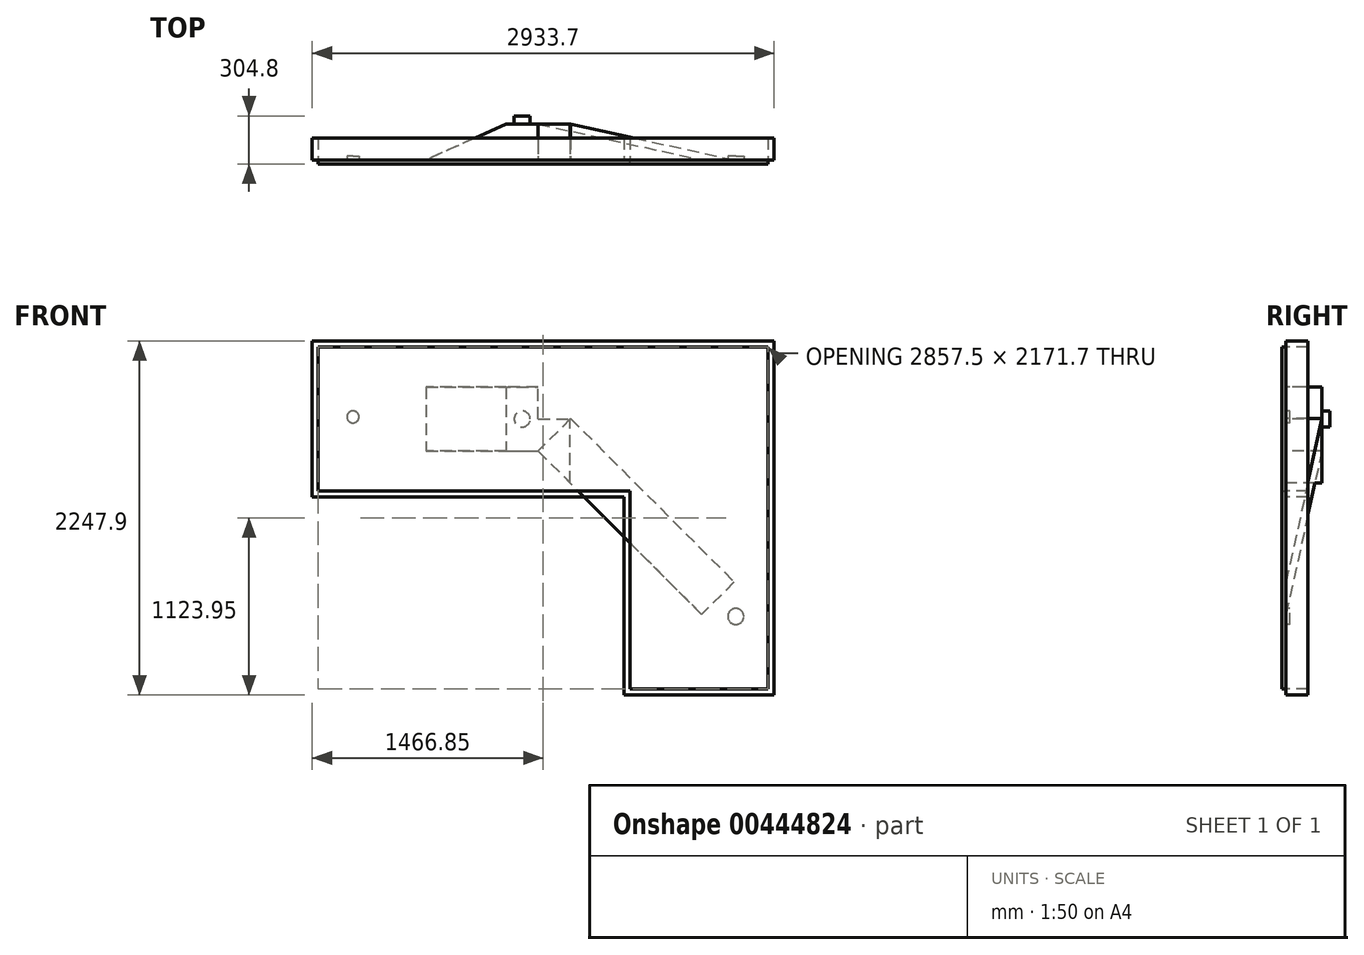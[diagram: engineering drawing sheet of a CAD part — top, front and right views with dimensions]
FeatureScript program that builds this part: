
annotation { "Feature Type Name" : "Feature", "Feature Type Description" : "" }
export const myFeature = defineFeature(function(context is Context, id is Id, definition is map)
    precondition{}
    {
        {
            var Q0;
            Q0=qCreatedBy(makeId("Front.planeOp"),FACE);
            var sketch = newSketch(context, id + "F0", { "sketchPlane" : qUnion([Q0])});
            skLineSegment(sketch, "E0", {"start": v(0, 0) * mm, "end": v(0, -914.4) * mm});
            skLineSegment(sketch, "E1", {"start": v(0, -914.4) * mm, "end": v(0, -952.5) * mm});
            skLineSegment(sketch, "E2", {"start": v(0, -952.5) * mm, "end": v(152.4, -952.5) * mm});
            skLineSegment(sketch, "E3", {"start": v(152.4, -952.5) * mm, "end": v(152.4, 0) * mm});
            skLineSegment(sketch, "E4", {"start": v(152.4, 0) * mm, "end": v(0, 0) * mm});
            skLineSegment(sketch, "E5", {"start": v(152.4, 0) * mm, "end": v(152.4, 38.1) * mm});
            skLineSegment(sketch, "E6", {"start": v(152.4, 38.1) * mm, "end": v(0, 38.1) * mm});
            skLineSegment(sketch, "E7", {"start": v(0, 38.1) * mm, "end": v(0, 0) * mm});
            skLineSegment(sketch, "E8", {"start": v(0, 38.1) * mm, "end": v(-38.1, 38.1) * mm});
            skLineSegment(sketch, "E9", {"start": v(-38.1, 38.1) * mm, "end": v(-38.1, -952.5) * mm});
            skLineSegment(sketch, "E10", {"start": v(-38.1, -952.5) * mm, "end": v(0, -952.5) * mm});
            skLineSegment(sketch, "E11", {"start": v(0, -914.4) * mm, "end": v(152.4, -914.4) * mm});
            skSolve(sketch);
        }
        {
            var Q0;
            Q0=makeQuery(id+"F0.imprint","IMPRINT",FACE,{"disambiguationData":[TD([[makeQuery(id+"F0.imprint","IMPRINT",EDGE,{"derivedFrom":sQuery(id+"F0.wireOp",EDGE,"E1")}),1.0]])]});
            var Q1;
            Q1=makeQuery(id+"F0.imprint","IMPRINT",FACE,{"disambiguationData":[TD([[makeQuery(id+"F0.imprint","IMPRINT",EDGE,{"derivedFrom":sQuery(id+"F0.wireOp",EDGE,"E0")}),-1.0]])]});
            var Q2;
            Q2=makeQuery(id+"F0.imprint","IMPRINT",FACE,{"disambiguationData":[TD([[makeQuery(id+"F0.imprint","IMPRINT",EDGE,{"derivedFrom":sQuery(id+"F0.wireOp",EDGE,"E4")}),-1.0]])]});
            extrude(context, id + "F1", {"entities" : qUnion([Q0, Q1, Q2]), "oppositeDirection" : true, "depth" : 139.7 * mm});
        }
        {
            var Q0;
            Q0=makeQuery(id+"F1.opExtrude","CAP_FACE",FACE,{"disambiguationData":[OSD([sQuery(id+"F0.wireOp",EDGE,"E0"),sQuery(id+"F0.wireOp",EDGE,"E2"),sQuery(id+"F0.wireOp",EDGE,"E3"),sQuery(id+"F0.wireOp",EDGE,"E4"),sQuery(id+"F0.wireOp",EDGE,"E5"),sQuery(id+"F0.wireOp",EDGE,"E6"),sQuery(id+"F0.wireOp",EDGE,"E8"),sQuery(id+"F0.wireOp",EDGE,"E9"),sQuery(id+"F0.wireOp",EDGE,"E10"),sQuery(id+"F0.wireOp",EDGE,"E11")])],"isStart":true});
            var sketch = newSketch(context, id + "F2", { "sketchPlane" : qUnion([Q0])});
            skLineSegment(sketch, "E12", {"start": v(152.4, 38.1) * mm, "end": v(152.4, 0) * mm});
            skLineSegment(sketch, "E13", {"start": v(152.4, 0) * mm, "end": v(2895.6, 0) * mm});
            skLineSegment(sketch, "E14", {"start": v(2895.6, 0) * mm, "end": v(2895.6, 38.1) * mm});
            skLineSegment(sketch, "E15", {"start": v(2895.6, 38.1) * mm, "end": v(152.4, 38.1) * mm});
            skLineSegment(sketch, "E16", {"start": v(2895.6, 0) * mm, "end": v(2895.6, -914.4) * mm});
            skLineSegment(sketch, "E17", {"start": v(2895.6, -914.4) * mm, "end": v(2895.6, -952.5) * mm});
            skLineSegment(sketch, "E18", {"start": v(2895.6, -952.5) * mm, "end": v(152.4, -952.5) * mm});
            skLineSegment(sketch, "E19", {"start": v(152.4, -952.5) * mm, "end": v(152.4, -914.4) * mm});
            skLineSegment(sketch, "E20", {"start": v(152.4, -914.4) * mm, "end": v(2895.6, -914.4) * mm});
            skLineSegment(sketch, "E21", {"start": v(2895.6, -914.4) * mm, "end": v(2857.5, -914.4) * mm});
            skLineSegment(sketch, "E22", {"start": v(2857.5, -914.4) * mm, "end": v(2857.5, 0) * mm});
            skLineSegment(sketch, "E23", {"start": v(2857.5, 0) * mm, "end": v(2895.6, 0) * mm});
            skSolve(sketch);
        }
        {
            var Q0;
            Q0=makeQuery(id+"F2.imprint","IMPRINT",FACE,{"disambiguationData":[TD([[makeQuery(id+"F2.imprint","IMPRINT",EDGE,{"derivedFrom":sQuery(id+"F2.wireOp",EDGE,"E16")}),-1.0]])]});
            var Q1;
            Q1=makeQuery(id+"F2.imprint","IMPRINT",FACE,{"disambiguationData":[TD([[makeQuery(id+"F2.imprint","IMPRINT",EDGE,{"derivedFrom":sQuery(id+"F2.wireOp",EDGE,"E12")}),-1.0]])]});
            extrude(context, id + "F3", {"entities" : qUnion([Q0, Q1]), "operationType" : NewBodyOperationType.ADD, "oppositeDirection" : true, "depth" : 139.7 * mm});
        }
        {
            var Q0;
            Q0=makeQuery(id+"F3.boolean.opBoolean","MERGE",FACE,{"derivedFrom":[makeQuery(id+"F1.opExtrude","CAP_FACE",FACE,{"disambiguationData":[OSD([sQuery(id+"F0.wireOp",EDGE,"E0"),sQuery(id+"F0.wireOp",EDGE,"E2"),sQuery(id+"F0.wireOp",EDGE,"E3"),sQuery(id+"F0.wireOp",EDGE,"E4"),sQuery(id+"F0.wireOp",EDGE,"E5"),sQuery(id+"F0.wireOp",EDGE,"E6"),sQuery(id+"F0.wireOp",EDGE,"E8"),sQuery(id+"F0.wireOp",EDGE,"E9"),sQuery(id+"F0.wireOp",EDGE,"E10"),sQuery(id+"F0.wireOp",EDGE,"E11")])],"isStart":true}),makeQuery(id+"F3.opExtrude","CAP_FACE",FACE,{"disambiguationData":[OSD([sQuery(id+"F2.wireOp",EDGE,"E12"),sQuery(id+"F2.wireOp",EDGE,"E13"),sQuery(id+"F2.wireOp",EDGE,"E14"),sQuery(id+"F2.wireOp",EDGE,"E15"),sQuery(id+"F2.wireOp",EDGE,"E16"),sQuery(id+"F2.wireOp",EDGE,"E21"),sQuery(id+"F2.wireOp",EDGE,"E22")])],"isStart":true})]});
            var sketch = newSketch(context, id + "F4", { "sketchPlane" : qUnion([Q0])});
            skLineSegment(sketch, "E24", {"start": v(152.4, -952.5) * mm, "end": v(1981.2, -952.5) * mm});
            skLineSegment(sketch, "E25", {"start": v(1981.2, -952.5) * mm, "end": v(1981.2, -914.4) * mm});
            skLineSegment(sketch, "E26", {"start": v(1981.2, -914.4) * mm, "end": v(152.4, -914.4) * mm});
            skLineSegment(sketch, "E27", {"start": v(152.4, -914.4) * mm, "end": v(152.4, -952.5) * mm});
            skSolve(sketch);
        }
        {
            var Q0;
            Q0=makeQuery(id+"F4.imprint","IMPRINT",FACE,{"disambiguationData":[TD([[makeQuery(id+"F4.imprint","IMPRINT",EDGE,{"derivedFrom":sQuery(id+"F4.wireOp",EDGE,"E24")}),1.0]])]});
            extrude(context, id + "F5", {"entities" : qUnion([Q0]), "operationType" : NewBodyOperationType.ADD, "oppositeDirection" : true, "depth" : 139.7 * mm});
        }
        {
            var Q0;
            Q0=makeQuery(id+"F5.boolean.opBoolean","MERGE",FACE,{"derivedFrom":[makeQuery(id+"F3.boolean.opBoolean","MERGE",FACE,{"derivedFrom":[makeQuery(id+"F1.opExtrude","CAP_FACE",FACE,{"disambiguationData":[OSD([sQuery(id+"F0.wireOp",EDGE,"E0"),sQuery(id+"F0.wireOp",EDGE,"E2"),sQuery(id+"F0.wireOp",EDGE,"E3"),sQuery(id+"F0.wireOp",EDGE,"E4"),sQuery(id+"F0.wireOp",EDGE,"E5"),sQuery(id+"F0.wireOp",EDGE,"E6"),sQuery(id+"F0.wireOp",EDGE,"E8"),sQuery(id+"F0.wireOp",EDGE,"E9"),sQuery(id+"F0.wireOp",EDGE,"E10"),sQuery(id+"F0.wireOp",EDGE,"E11")])],"isStart":true}),makeQuery(id+"F3.opExtrude","CAP_FACE",FACE,{"disambiguationData":[OSD([sQuery(id+"F2.wireOp",EDGE,"E12"),sQuery(id+"F2.wireOp",EDGE,"E13"),sQuery(id+"F2.wireOp",EDGE,"E14"),sQuery(id+"F2.wireOp",EDGE,"E15"),sQuery(id+"F2.wireOp",EDGE,"E16"),sQuery(id+"F2.wireOp",EDGE,"E21"),sQuery(id+"F2.wireOp",EDGE,"E22")])],"isStart":true})]}),makeQuery(id+"F5.opExtrude","CAP_FACE",FACE,{"disambiguationData":[OSD([sQuery(id+"F4.wireOp",EDGE,"E24"),sQuery(id+"F4.wireOp",EDGE,"E25"),sQuery(id+"F4.wireOp",EDGE,"E26"),sQuery(id+"F4.wireOp",EDGE,"E27")])],"isStart":true})]});
            var sketch = newSketch(context, id + "F6", { "sketchPlane" : qUnion([Q0])});
            skLineSegment(sketch, "E28", {"start": v(1981.2, -952.5) * mm, "end": v(1981.2, -2171.7) * mm});
            skLineSegment(sketch, "E29", {"start": v(1981.2, -2171.7) * mm, "end": v(1943.1, -2171.7) * mm});
            skLineSegment(sketch, "E30", {"start": v(1943.1, -2171.7) * mm, "end": v(1943.1, -952.5) * mm});
            skLineSegment(sketch, "E31", {"start": v(1943.1, -952.5) * mm, "end": v(1981.2, -952.5) * mm});
            skLineSegment(sketch, "E32", {"start": v(1981.2, -2171.7) * mm, "end": v(2857.5, -2171.7) * mm});
            skLineSegment(sketch, "E33", {"start": v(2857.5, -2171.7) * mm, "end": v(2895.6, -2171.7) * mm});
            skLineSegment(sketch, "E34", {"start": v(2895.6, -2171.7) * mm, "end": v(2895.6, -914.4) * mm});
            skLineSegment(sketch, "E35", {"start": v(2895.6, -914.4) * mm, "end": v(2857.5, -914.4) * mm});
            skLineSegment(sketch, "E36", {"start": v(2857.5, -914.4) * mm, "end": v(2857.5, -2171.7) * mm});
            skLineSegment(sketch, "E37", {"start": v(1943.1, -2171.7) * mm, "end": v(1943.1, -2209.8) * mm});
            skLineSegment(sketch, "E38", {"start": v(1943.1, -2209.8) * mm, "end": v(2895.6, -2209.8) * mm});
            skLineSegment(sketch, "E39", {"start": v(2895.6, -2209.8) * mm, "end": v(2895.6, -2171.7) * mm});
            skSolve(sketch);
        }
        {
            var Q0;
            Q0=makeQuery(id+"F6.imprint","IMPRINT",FACE,{"disambiguationData":[TD([[makeQuery(id+"F6.imprint","IMPRINT",EDGE,{"derivedFrom":sQuery(id+"F6.wireOp",EDGE,"E33")}),1.0]])]});
            var Q1;
            Q1=makeQuery(id+"F6.imprint","IMPRINT",FACE,{"disambiguationData":[TD([[makeQuery(id+"F6.imprint","IMPRINT",EDGE,{"derivedFrom":sQuery(id+"F6.wireOp",EDGE,"E29")}),1.0]])]});
            var Q2;
            Q2=makeQuery(id+"F6.imprint","IMPRINT",FACE,{"disambiguationData":[TD([[makeQuery(id+"F6.imprint","IMPRINT",EDGE,{"derivedFrom":sQuery(id+"F6.wireOp",EDGE,"E28")}),-1.0]])]});
            extrude(context, id + "F7", {"entities" : qUnion([Q0, Q1, Q2]), "operationType" : NewBodyOperationType.ADD, "oppositeDirection" : true, "depth" : 139.7 * mm});
        }
        {
            var Q0;
            Q0=makeQuery(id+"F7.boolean.opBoolean","MERGE",FACE,{"derivedFrom":[makeQuery(id+"F5.boolean.opBoolean","MERGE",FACE,{"derivedFrom":[makeQuery(id+"F3.boolean.opBoolean","MERGE",FACE,{"derivedFrom":[makeQuery(id+"F1.opExtrude","CAP_FACE",FACE,{"disambiguationData":[OSD([sQuery(id+"F0.wireOp",EDGE,"E0"),sQuery(id+"F0.wireOp",EDGE,"E2"),sQuery(id+"F0.wireOp",EDGE,"E3"),sQuery(id+"F0.wireOp",EDGE,"E4"),sQuery(id+"F0.wireOp",EDGE,"E5"),sQuery(id+"F0.wireOp",EDGE,"E6"),sQuery(id+"F0.wireOp",EDGE,"E8"),sQuery(id+"F0.wireOp",EDGE,"E9"),sQuery(id+"F0.wireOp",EDGE,"E10"),sQuery(id+"F0.wireOp",EDGE,"E11")])],"isStart":true}),makeQuery(id+"F3.opExtrude","CAP_FACE",FACE,{"disambiguationData":[OSD([sQuery(id+"F2.wireOp",EDGE,"E12"),sQuery(id+"F2.wireOp",EDGE,"E13"),sQuery(id+"F2.wireOp",EDGE,"E14"),sQuery(id+"F2.wireOp",EDGE,"E15"),sQuery(id+"F2.wireOp",EDGE,"E16"),sQuery(id+"F2.wireOp",EDGE,"E21"),sQuery(id+"F2.wireOp",EDGE,"E22")])],"isStart":true})]}),makeQuery(id+"F5.opExtrude","CAP_FACE",FACE,{"disambiguationData":[OSD([sQuery(id+"F4.wireOp",EDGE,"E24"),sQuery(id+"F4.wireOp",EDGE,"E25"),sQuery(id+"F4.wireOp",EDGE,"E26"),sQuery(id+"F4.wireOp",EDGE,"E27")])],"isStart":true})]}),makeQuery(id+"F7.opExtrude","CAP_FACE",FACE,{"disambiguationData":[OSD([sQuery(id+"F6.wireOp",EDGE,"E28"),sQuery(id+"F6.wireOp",EDGE,"E30"),sQuery(id+"F6.wireOp",EDGE,"E31"),sQuery(id+"F6.wireOp",EDGE,"E32"),sQuery(id+"F6.wireOp",EDGE,"E34"),sQuery(id+"F6.wireOp",EDGE,"E35"),sQuery(id+"F6.wireOp",EDGE,"E36"),sQuery(id+"F6.wireOp",EDGE,"E37"),sQuery(id+"F6.wireOp",EDGE,"E38"),sQuery(id+"F6.wireOp",EDGE,"E39")])],"isStart":true})]});
            var sketch = newSketch(context, id + "F8", { "sketchPlane" : qUnion([Q0])});
            skLineSegment(sketch, "E40", {"start": v(2895.6, 38.1) * mm, "end": v(-38.1, 38.1) * mm});
            skLineSegment(sketch, "E41", {"start": v(-38.1, 38.1) * mm, "end": v(-38.1, -952.5) * mm});
            skLineSegment(sketch, "E42", {"start": v(-38.1, -952.5) * mm, "end": v(1943.1, -952.5) * mm});
            skLineSegment(sketch, "E43", {"start": v(1943.1, -952.5) * mm, "end": v(1943.1, -2209.8) * mm});
            skLineSegment(sketch, "E44", {"start": v(1943.1, -2209.8) * mm, "end": v(2895.6, -2209.8) * mm});
            skLineSegment(sketch, "E45", {"start": v(2895.6, -2209.8) * mm, "end": v(2895.6, 38.1) * mm});
            skSolve(sketch);
        }
        {
            var Q0;
            Q0=makeQuery(id+"F8.imprint","IMPRINT",FACE,{"disambiguationData":[TD([[makeQuery(id+"F8.imprint","IMPRINT",EDGE,{"derivedFrom":makeQuery(id+"F1.opExtrude","CAP_EDGE",EDGE,{"disambiguationData":[OSD([sQuery(id+"F0.wireOp",EDGE,"E0")])],"isStart":true})}),1.0]])]});
            extrude(context, id + "F9", {"entities" : qUnion([Q0]), "depth" : 25.4 * mm});
        }
        {
            var Q0;
            Q0=makeQuery(id+"F5.boolean.opBoolean","MERGE",FACE,{"derivedFrom":[makeQuery(id+"F1.opExtrude","SWEPT_FACE",FACE,{"disambiguationData":[OSD([sQuery(id+"F0.wireOp",EDGE,"E11")])]}),makeQuery(id+"F5.opExtrude","SWEPT_FACE",FACE,{"disambiguationData":[OSD([sQuery(id+"F4.wireOp",EDGE,"E26")])]})]});
            var sketch = newSketch(context, id + "F10", { "sketchPlane" : qUnion([Q0])});
            skLineSegment(sketch, "E46", {"start": v(0, 0) * mm, "end": v(990.6, 0) * mm});
            skLineSegment(sketch, "E47", {"start": v(990.6, 0) * mm, "end": v(1193.8, 0) * mm});
            skLineSegment(sketch, "E48", {"start": v(1193.8, 0) * mm, "end": v(685.8, 0) * mm});
            skLineSegment(sketch, "E49", {"start": v(1193.8, 0) * mm, "end": v(1193.8, 228.6) * mm});
            skLineSegment(sketch, "E50", {"start": v(1193.8, 228.6) * mm, "end": v(685.8, 0) * mm});
            skSolve(sketch);
        }
        {
            var Q0;
            Q0 = qSketchRegion(id + "F10", true);
            extrude(context, id + "F11", {"entities" : qUnion([Q0]), "operationType" : NewBodyOperationType.ADD, "depth" : 660.4 * mm, "hasSecondDirection" : true, "secondDirectionOppositeDirection" : false, "secondDirectionDepth" : 254 * mm});
        }
        {
            var Q0;
            Q0=makeQuery(id+"F9.opExtrude","CAP_FACE",FACE,{"disambiguationData":[OSD([sQuery(id+"F0.wireOp",EDGE,"E0"),sQuery(id+"F0.wireOp",EDGE,"E4"),sQuery(id+"F0.wireOp",EDGE,"E11"),sQuery(id+"F2.wireOp",EDGE,"E13"),sQuery(id+"F2.wireOp",EDGE,"E22"),sQuery(id+"F4.wireOp",EDGE,"E25"),sQuery(id+"F4.wireOp",EDGE,"E26"),sQuery(id+"F6.wireOp",EDGE,"E28"),sQuery(id+"F6.wireOp",EDGE,"E32"),sQuery(id+"F6.wireOp",EDGE,"E36")])],"isStart":true});
            var sketch = newSketch(context, id + "F12", { "sketchPlane" : qUnion([Q0])});
            skLineSegment(sketch, "E51", {"start": v(-1193.8, -660.4) * mm, "end": v(-1320.8, -660.4) * mm});
            skLineSegment(sketch, "E52", {"start": v(-1320.8, -660.4) * mm, "end": v(-1397, -660.4) * mm});
            skLineSegment(sketch, "E53", {"start": v(-1397, -660.4) * mm, "end": v(-1397, -254) * mm});
            skLineSegment(sketch, "E54", {"start": v(-1397, -254) * mm, "end": v(-1193.8, -254) * mm});
            skLineSegment(sketch, "E55", {"start": v(-1193.8, -254) * mm, "end": v(-1193.8, -660.4) * mm});
            skSolve(sketch);
        }
        {
            var Q0;
            Q0 = qSketchRegion(id + "F12", true);
            extrude(context, id + "F13", {"entities" : qUnion([Q0]), "operationType" : NewBodyOperationType.ADD, "depth" : 228.6 * mm});
        }
        {
            var Q0;
            Q0=makeQuery(id+"F13.opExtrude","CAP_FACE",FACE,{"disambiguationData":[OSD([sQuery(id+"F12.wireOp",EDGE,"E51"),sQuery(id+"F12.wireOp",EDGE,"E52"),sQuery(id+"F12.wireOp",EDGE,"E53"),sQuery(id+"F12.wireOp",EDGE,"E54"),sQuery(id+"F12.wireOp",EDGE,"E55")])],"isStart":false});
            var sketch = newSketch(context, id + "F14", { "sketchPlane" : qUnion([Q0])});
            skLineSegment(sketch, "E56", {"start": v(-1193.8, -457.2) * mm, "end": v(-1397, -457.2) * mm});
            skCircle(sketch, "E57", {"center": v(-1295.4, -457.2) * mm, "radius": 50.8 * mm});
            skSolve(sketch);
        }
        {
            var Q0;
            Q0 = qSketchRegion(id + "F14", true);
            extrude(context, id + "F15", {"entities" : qUnion([Q0]), "operationType" : NewBodyOperationType.ADD, "depth" : 50.8 * mm});
        }
        {
            var Q0;
            Q0=makeQuery(id+"F9.opExtrude","CAP_FACE",FACE,{"disambiguationData":[OSD([sQuery(id+"F0.wireOp",EDGE,"E0"),sQuery(id+"F0.wireOp",EDGE,"E4"),sQuery(id+"F0.wireOp",EDGE,"E11"),sQuery(id+"F2.wireOp",EDGE,"E13"),sQuery(id+"F2.wireOp",EDGE,"E22"),sQuery(id+"F4.wireOp",EDGE,"E25"),sQuery(id+"F4.wireOp",EDGE,"E26"),sQuery(id+"F6.wireOp",EDGE,"E28"),sQuery(id+"F6.wireOp",EDGE,"E32"),sQuery(id+"F6.wireOp",EDGE,"E36")])],"isStart":true});
            var sketch = newSketch(context, id + "F16", { "sketchPlane" : qUnion([Q0])});
            skLineSegment(sketch, "E58", {"start": v(-1397, -660.4) * mm, "end": v(-1397, -457.2) * mm});
            skLineSegment(sketch, "E59", {"start": v(-1397, -457.2) * mm, "end": v(-1600.2, -457.2) * mm});
            skLineSegment(sketch, "E60", {"start": v(-1600.2, -457.2) * mm, "end": v(-1397, -660.4) * mm});
            skSolve(sketch);
        }
        {
            var Q0;
            Q0=makeQuery(id+"F9.opExtrude","CAP_FACE",FACE,{"disambiguationData":[OSD([sQuery(id+"F0.wireOp",EDGE,"E0"),sQuery(id+"F0.wireOp",EDGE,"E4"),sQuery(id+"F0.wireOp",EDGE,"E11"),sQuery(id+"F2.wireOp",EDGE,"E13"),sQuery(id+"F2.wireOp",EDGE,"E22"),sQuery(id+"F4.wireOp",EDGE,"E25"),sQuery(id+"F4.wireOp",EDGE,"E26"),sQuery(id+"F6.wireOp",EDGE,"E28"),sQuery(id+"F6.wireOp",EDGE,"E32"),sQuery(id+"F6.wireOp",EDGE,"E36")])],"isStart":true});
            var sketch = newSketch(context, id + "F17", { "sketchPlane" : qUnion([Q0])});
            skLineSegment(sketch, "E61", {"start": v(-1600.2, -660.4) * mm, "end": v(-1600.2, -457.2) * mm});
            skLineSegment(sketch, "E62", {"start": v(-1397, -660.4) * mm, "end": v(-1600.2, -457.2) * mm});
            skLineSegment(sketch, "E63", {"start": v(-1397, -660.4) * mm, "end": v(-1600.2, -863.6) * mm});
            skLineSegment(sketch, "E64", {"start": v(-1600.2, -863.6) * mm, "end": v(-1600.2, -660.4) * mm});
            skSolve(sketch);
        }
        {
            var Q0;
            Q0 = qSketchRegion(id + "F16", true);
            extrude(context, id + "F18", {"entities" : qUnion([Q0]), "operationType" : NewBodyOperationType.ADD, "depth" : 228.6 * mm});
        }
        {
            var Q0;
            Q0 = qSketchRegion(id + "F17", true);
            extrude(context, id + "F19", {"entities" : qUnion([Q0]), "operationType" : NewBodyOperationType.ADD, "depth" : 228.6 * mm});
        }
        {
            var Q0;
            Q0=makeQuery(id+"F19.opExtrude","SWEPT_FACE",FACE,{"disambiguationData":[OSD([sQuery(id+"F17.wireOp",EDGE,"E63")])]});
            var sketch = newSketch(context, id + "F20", { "sketchPlane" : qUnion([Q0])});
            skLineSegment(sketch, "E65", {"start": v(0, -1742.17) * mm, "end": v(0, -2923.35) * mm});
            skLineSegment(sketch, "E66", {"start": v(0, -1454.8) * mm, "end": v(0, -1742.17) * mm});
            skLineSegment(sketch, "E67", {"start": v(0, -1454.8) * mm, "end": v(-228.6, -1454.8) * mm});
            skLineSegment(sketch, "E68", {"start": v(-228.6, -1454.8) * mm, "end": v(0, -2923.35) * mm});
            skSolve(sketch);
        }
        {
            var Q0;
            Q0 = qSketchRegion(id + "F20", true);
            extrude(context, id + "F21", {"entities" : qUnion([Q0]), "oppositeDirection" : true, "depth" : 292.1 * mm});
        }
        {
            var Q0;
            Q0=makeQuery(id+"F9.opExtrude","CAP_FACE",FACE,{"disambiguationData":[OSD([sQuery(id+"F0.wireOp",EDGE,"E0"),sQuery(id+"F0.wireOp",EDGE,"E4"),sQuery(id+"F0.wireOp",EDGE,"E11"),sQuery(id+"F2.wireOp",EDGE,"E13"),sQuery(id+"F2.wireOp",EDGE,"E22"),sQuery(id+"F4.wireOp",EDGE,"E25"),sQuery(id+"F4.wireOp",EDGE,"E26"),sQuery(id+"F6.wireOp",EDGE,"E28"),sQuery(id+"F6.wireOp",EDGE,"E32"),sQuery(id+"F6.wireOp",EDGE,"E36")])],"isStart":true});
            var sketch = newSketch(context, id + "F22", { "sketchPlane" : qUnion([Q0])});
            skCircle(sketch, "E69", {"center": v(-2652.5, -1711.68) * mm, "radius": 50.8 * mm});
            skSolve(sketch);
        }
        {
            var Q0;
            Q0 = qSketchRegion(id + "F22", true);
            extrude(context, id + "F23", {"entities" : qUnion([Q0]), "operationType" : NewBodyOperationType.ADD, "depth" : 25.4 * mm});
        }
        {
            var Q0;
            Q0=makeQuery(id+"F9.opExtrude","CAP_FACE",FACE,{"disambiguationData":[OSD([sQuery(id+"F0.wireOp",EDGE,"E0"),sQuery(id+"F0.wireOp",EDGE,"E4"),sQuery(id+"F0.wireOp",EDGE,"E11"),sQuery(id+"F2.wireOp",EDGE,"E13"),sQuery(id+"F2.wireOp",EDGE,"E22"),sQuery(id+"F4.wireOp",EDGE,"E25"),sQuery(id+"F4.wireOp",EDGE,"E26"),sQuery(id+"F6.wireOp",EDGE,"E28"),sQuery(id+"F6.wireOp",EDGE,"E32"),sQuery(id+"F6.wireOp",EDGE,"E36")])],"isStart":true});
            var sketch = newSketch(context, id + "F24", { "sketchPlane" : qUnion([Q0])});
            skCircle(sketch, "E70", {"center": v(-220.83, -444.03) * mm, "radius": 38.1 * mm});
            skSolve(sketch);
        }
        {
            var Q0;
            Q0 = qSketchRegion(id + "F24", true);
            extrude(context, id + "F25", {"entities" : qUnion([Q0]), "operationType" : NewBodyOperationType.ADD, "depth" : 25.4 * mm});
        }
    });
